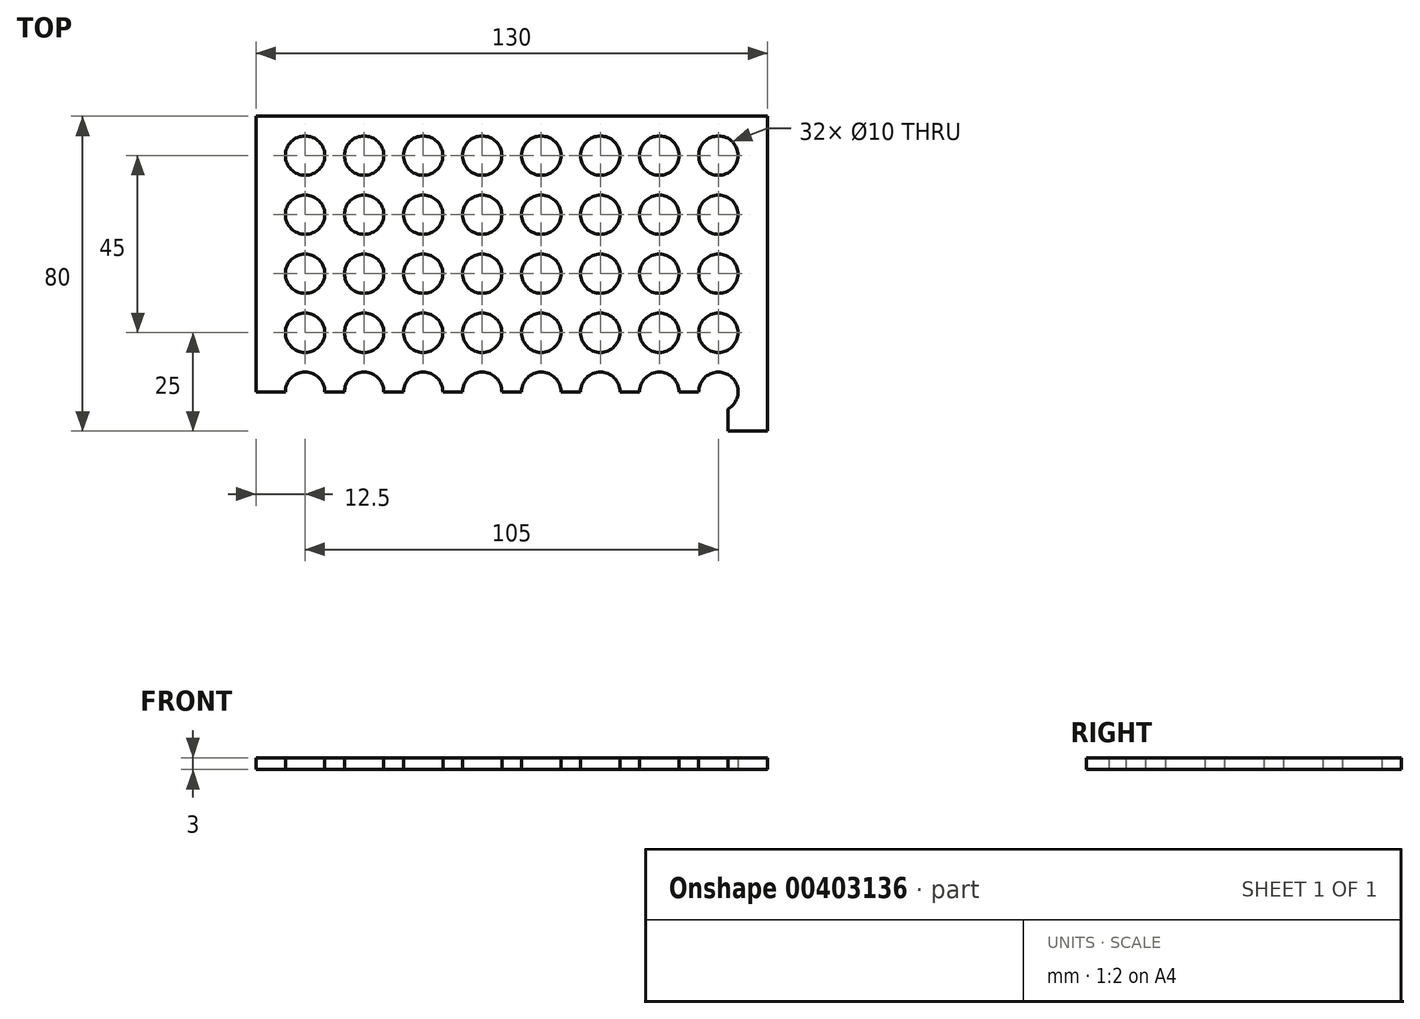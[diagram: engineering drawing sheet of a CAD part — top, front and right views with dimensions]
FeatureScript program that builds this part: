
annotation { "Feature Type Name" : "Feature", "Feature Type Description" : "" }
export const myFeature = defineFeature(function(context is Context, id is Id, definition is map)
    precondition{}
    {
        {
            var Q0;
            Q0=qCreatedBy(makeId("Top.planeOp"),FACE);
            var sketch = newSketch(context, id + "F0", { "sketchPlane" : qUnion([Q0])});
            skLineSegment(sketch, "E0.bottom", {"start": v(65, 40) * mm, "end": v(-65, 40) * mm});
            skLineSegment(sketch, "E0.top", {"start": v(65, -40) * mm, "end": v(-65, -40) * mm});
            skLineSegment(sketch, "E0.left", {"start": v(65, 40) * mm, "end": v(65, -40) * mm});
            skLineSegment(sketch, "E0.right", {"start": v(-65, 40) * mm, "end": v(-65, -40) * mm});
            skPoint(sketch, "E0.middle", {"position": v(0, 0) * mm});
            skCircle(sketch, "E1", {"center": v(-52.5, 30) * mm, "radius": 5 * mm});
            skLineSegment(sketch, "E2.0", {"start": v(-57.5, 40) * mm, "end": v(-57.5, -40) * mm, "construction": true});
            skLineSegment(sketch, "E3.0", {"start": v(-65.1, 40.11) * mm, "end": v(-65.1, -40) * mm});
            skLineSegment(sketch, "E4.0", {"start": v(65, 35) * mm, "end": v(-65, 35) * mm, "construction": true});
            skCircle(sketch, "E5.1.0.0", {"center": v(-52.5, 15) * mm, "radius": 5 * mm});
            skCircle(sketch, "E5.2.0.0", {"center": v(-52.5, 0) * mm, "radius": 5 * mm});
            skCircle(sketch, "E5.3.0.0", {"center": v(-52.5, -15) * mm, "radius": 5 * mm});
            skCircle(sketch, "E5.4.0.0", {"center": v(-52.5, -30) * mm, "radius": 5 * mm});
            skLineSegment(sketch, "E5.direction1", {"start": v(-52.5, 30) * mm, "end": v(-37.5, 30) * mm, "construction": true});
            skCircle(sketch, "E6.1.0.0", {"center": v(-37.5, 30) * mm, "radius": 5 * mm});
            skCircle(sketch, "E6.1.0.1", {"center": v(-37.5, 15) * mm, "radius": 5 * mm});
            skCircle(sketch, "E6.1.0.2", {"center": v(-37.5, 0) * mm, "radius": 5 * mm});
            skCircle(sketch, "E6.1.0.3", {"center": v(-37.5, -15) * mm, "radius": 5 * mm});
            skCircle(sketch, "E6.1.0.4", {"center": v(-37.5, -30) * mm, "radius": 5 * mm});
            skCircle(sketch, "E6.2.0.0", {"center": v(-22.5, 30) * mm, "radius": 5 * mm});
            skCircle(sketch, "E6.2.0.1", {"center": v(-22.5, 15) * mm, "radius": 5 * mm});
            skCircle(sketch, "E6.2.0.2", {"center": v(-22.5, 0) * mm, "radius": 5 * mm});
            skCircle(sketch, "E6.2.0.3", {"center": v(-22.5, -15) * mm, "radius": 5 * mm});
            skCircle(sketch, "E6.2.0.4", {"center": v(-22.5, -30) * mm, "radius": 5 * mm});
            skCircle(sketch, "E6.3.0.0", {"center": v(-7.5, 30) * mm, "radius": 5 * mm});
            skCircle(sketch, "E6.3.0.1", {"center": v(-7.5, 15) * mm, "radius": 5 * mm});
            skCircle(sketch, "E6.3.0.2", {"center": v(-7.5, 0) * mm, "radius": 5 * mm});
            skCircle(sketch, "E6.3.0.3", {"center": v(-7.5, -15) * mm, "radius": 5 * mm});
            skCircle(sketch, "E6.3.0.4", {"center": v(-7.5, -30) * mm, "radius": 5 * mm});
            skCircle(sketch, "E6.4.0.0", {"center": v(7.5, 30) * mm, "radius": 5 * mm});
            skCircle(sketch, "E6.4.0.1", {"center": v(7.5, 15) * mm, "radius": 5 * mm});
            skCircle(sketch, "E6.4.0.2", {"center": v(7.5, 0) * mm, "radius": 5 * mm});
            skCircle(sketch, "E6.4.0.3", {"center": v(7.5, -15) * mm, "radius": 5 * mm});
            skCircle(sketch, "E6.4.0.4", {"center": v(7.5, -30) * mm, "radius": 5 * mm});
            skCircle(sketch, "E6.5.0.0", {"center": v(22.5, 30) * mm, "radius": 5 * mm});
            skCircle(sketch, "E6.5.0.1", {"center": v(22.5, 15) * mm, "radius": 5 * mm});
            skCircle(sketch, "E6.5.0.2", {"center": v(22.5, 0) * mm, "radius": 5 * mm});
            skCircle(sketch, "E6.5.0.3", {"center": v(22.5, -15) * mm, "radius": 5 * mm});
            skCircle(sketch, "E6.5.0.4", {"center": v(22.5, -30) * mm, "radius": 5 * mm});
            skCircle(sketch, "E6.6.0.0", {"center": v(37.5, 30) * mm, "radius": 5 * mm});
            skCircle(sketch, "E6.6.0.1", {"center": v(37.5, 15) * mm, "radius": 5 * mm});
            skCircle(sketch, "E6.6.0.2", {"center": v(37.5, 0) * mm, "radius": 5 * mm});
            skCircle(sketch, "E6.6.0.3", {"center": v(37.5, -15) * mm, "radius": 5 * mm});
            skCircle(sketch, "E6.6.0.4", {"center": v(37.5, -30) * mm, "radius": 5 * mm});
            skCircle(sketch, "E6.7.0.0", {"center": v(52.5, 30) * mm, "radius": 5 * mm});
            skCircle(sketch, "E6.7.0.1", {"center": v(52.5, 15) * mm, "radius": 5 * mm});
            skCircle(sketch, "E6.7.0.2", {"center": v(52.5, 0) * mm, "radius": 5 * mm});
            skCircle(sketch, "E6.7.0.3", {"center": v(52.5, -15) * mm, "radius": 5 * mm});
            skCircle(sketch, "E6.7.0.4", {"center": v(52.5, -30) * mm, "radius": 5 * mm});
            skLineSegment(sketch, "E6.direction1", {"start": v(-52.5, -30) * mm, "end": v(-37.5, -30) * mm, "construction": true});
            skArc(sketch, "E7.0.startCap", {"start": v(65, 50) * mm, "mid": v(75, 40) * mm, "end": v(65, 30) * mm});
            skArc(sketch, "E7.0.endCap", {"start": v(-65, 30) * mm, "mid": v(-75, 40) * mm, "end": v(-65, 50) * mm});
            skLineSegment(sketch, "E7.0.left", {"start": v(65, 30) * mm, "end": v(-65, 30) * mm});
            skLineSegment(sketch, "E7.0.right", {"start": v(65, 50) * mm, "end": v(-65, 50) * mm});
            skArc(sketch, "E7.1.startCap", {"start": v(-75.1, 40.11) * mm, "mid": v(-65.1, 50.11) * mm, "end": v(-55.1, 40.11) * mm});
            skArc(sketch, "E7.1.endCap", {"start": v(-55.1, -40) * mm, "mid": v(-65.1, -50) * mm, "end": v(-75.1, -40) * mm});
            skLineSegment(sketch, "E7.1.left", {"start": v(-55.1, 40.11) * mm, "end": v(-55.1, -40) * mm});
            skLineSegment(sketch, "E7.1.right", {"start": v(-75.1, 40.11) * mm, "end": v(-75.1, -40) * mm});
            skArc(sketch, "E7.2.startCap", {"start": v(55, 40) * mm, "mid": v(65, 50) * mm, "end": v(75, 40) * mm});
            skArc(sketch, "E7.2.endCap", {"start": v(75, -40) * mm, "mid": v(65, -50) * mm, "end": v(55, -40) * mm});
            skLineSegment(sketch, "E7.2.left", {"start": v(75, 40) * mm, "end": v(75, -40) * mm});
            skLineSegment(sketch, "E7.2.right", {"start": v(55, 40) * mm, "end": v(55, -40) * mm});
            skArc(sketch, "E7.3.startCap", {"start": v(65, -30) * mm, "mid": v(75, -40) * mm, "end": v(65, -50) * mm});
            skArc(sketch, "E7.3.endCap", {"start": v(-65, -50) * mm, "mid": v(-75, -40) * mm, "end": v(-65, -30) * mm});
            skLineSegment(sketch, "E7.3.left", {"start": v(65, -50) * mm, "end": v(-65, -50) * mm});
            skLineSegment(sketch, "E7.3.right", {"start": v(65, -30) * mm, "end": v(-65, -30) * mm});
            skSolve(sketch);
        }
        {
            var Q0;
            {var subQ7=sQuery(id+"F0.wireOp",EDGE,"E1");var subQ17=sQuery(id+"F0.wireOp",EDGE,"E7.1.left");var subQ26=makeQuery(id+"F0.imprint","INTERSECT",VERTEX,{"disambiguationData":[OD(0.0)],"derivedFrom":[subQ7,subQ17]});Q0=makeQuery(id+"F0.imprint","IMPRINT",FACE,{"disambiguationData":[TD([[makeQuery(id+"F0.imprint","IMPRINT",EDGE,{"disambiguationData":[TD([[subQ26,1.0]])],"derivedFrom":subQ7}),-1.0]])]});}
            var Q1;
            {var subQ1=sQuery(id+"F0.wireOp",EDGE,"E3.0");var subQ5=sQuery(id+"F0.wireOp",EDGE,"E0.bottom");var subQ6=makeQuery(id+"F0.imprint","INTERSECT",VERTEX,{"derivedFrom":[subQ5,subQ1]});Q1=makeQuery(id+"F0.imprint","IMPRINT",FACE,{"disambiguationData":[TD([[makeQuery(id+"F0.imprint","IMPRINT",EDGE,{"disambiguationData":[TD([[subQ6,1.0]])],"derivedFrom":subQ5}),1.0]])]});}
            var Q2;
            {var subQ0=sQuery(id+"F0.wireOp",EDGE,"E7.0.left");var subQ3=sQuery(id+"F0.wireOp",EDGE,"E1");var subQ4=makeQuery(id+"F0.imprint","INTERSECT",VERTEX,{"disambiguationData":[OD(1.0)],"derivedFrom":[subQ3,subQ0]});Q2=makeQuery(id+"F0.imprint","IMPRINT",FACE,{"disambiguationData":[TD([[makeQuery(id+"F0.imprint","IMPRINT",EDGE,{"disambiguationData":[TD([[subQ4,-1.0]])],"derivedFrom":subQ3}),-1.0]])]});}
            var Q3;
            Q3=makeQuery(id+"F0.imprint","IMPRINT",FACE,{"disambiguationData":[TD([[makeQuery(id+"F0.imprint","IMPRINT",EDGE,{"derivedFrom":sQuery(id+"F0.wireOp",EDGE,"E6.1.0.1")}),-1.0]])]});
            var Q4;
            {var subQ5=sQuery(id+"F0.wireOp",EDGE,"E6.7.0.0");var subQ10=sQuery(id+"F0.wireOp",EDGE,"E7.0.left");var subQ20=makeQuery(id+"F0.imprint","INTERSECT",VERTEX,{"disambiguationData":[OD(0.0)],"derivedFrom":[subQ5,subQ10]});Q4=makeQuery(id+"F0.imprint","IMPRINT",FACE,{"disambiguationData":[TD([[makeQuery(id+"F0.imprint","IMPRINT",EDGE,{"disambiguationData":[TD([[subQ20,1.0]])],"derivedFrom":subQ5}),-1.0]])]});}
            var Q5;
            {var subQ0=sQuery(id+"F0.wireOp",EDGE,"E7.0.left");var subQ1=sQuery(id+"F0.wireOp",EDGE,"E6.7.0.0");var subQ2=makeQuery(id+"F0.imprint","INTERSECT",VERTEX,{"disambiguationData":[OD(0.0)],"derivedFrom":[subQ1,subQ0]});Q5=makeQuery(id+"F0.imprint","IMPRINT",FACE,{"disambiguationData":[TD([[makeQuery(id+"F0.imprint","IMPRINT",EDGE,{"disambiguationData":[TD([[subQ2,-1.0]])],"derivedFrom":subQ1}),-1.0]])]});}
            var Q6;
            {var subQ3=sQuery(id+"F0.wireOp",EDGE,"E6.7.0.4");var subQ5=sQuery(id+"F0.wireOp",EDGE,"E7.3.right");var subQ6=makeQuery(id+"F0.imprint","INTERSECT",VERTEX,{"disambiguationData":[OD(0.0)],"derivedFrom":[subQ3,subQ5]});Q6=makeQuery(id+"F0.imprint","IMPRINT",FACE,{"disambiguationData":[TD([[makeQuery(id+"F0.imprint","IMPRINT",EDGE,{"disambiguationData":[TD([[subQ6,1.0]])],"derivedFrom":subQ3}),-1.0]])]});}
            var Q7;
            {var subQ3=sQuery(id+"F0.wireOp",EDGE,"E5.4.0.0");var subQ5=sQuery(id+"F0.wireOp",EDGE,"E7.3.right");var subQ26=makeQuery(id+"F0.imprint","INTERSECT",VERTEX,{"disambiguationData":[OD(0.0)],"derivedFrom":[subQ3,subQ5]});Q7=makeQuery(id+"F0.imprint","IMPRINT",FACE,{"disambiguationData":[TD([[makeQuery(id+"F0.imprint","IMPRINT",EDGE,{"disambiguationData":[TD([[subQ26,1.0]])],"derivedFrom":subQ3}),-1.0]])]});}
            var Q8;
            {var subQ3=sQuery(id+"F0.wireOp",EDGE,"E5.4.0.0");var subQ5=sQuery(id+"F0.wireOp",EDGE,"E7.3.right");var subQ6=makeQuery(id+"F0.imprint","INTERSECT",VERTEX,{"disambiguationData":[OD(1.0)],"derivedFrom":[subQ3,subQ5]});Q8=makeQuery(id+"F0.imprint","IMPRINT",FACE,{"disambiguationData":[TD([[makeQuery(id+"F0.imprint","IMPRINT",EDGE,{"disambiguationData":[TD([[subQ6,-1.0]])],"derivedFrom":subQ3}),-1.0]])]});}
            extrude(context, id + "F1", {"entities" : qUnion([Q0, Q1, Q2, Q3, Q4, Q5, Q6, Q7, Q8]), "depth" : 3 * mm});
        }
    });
